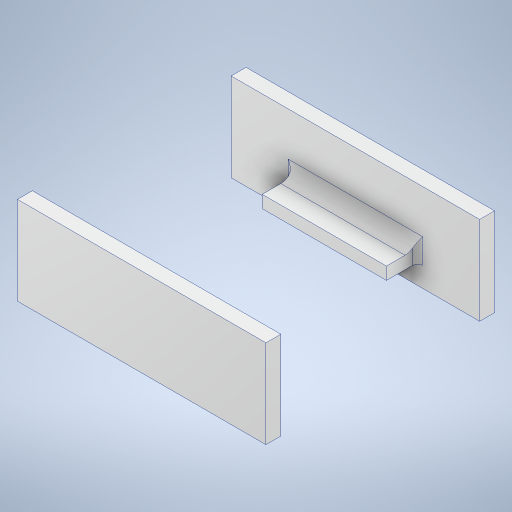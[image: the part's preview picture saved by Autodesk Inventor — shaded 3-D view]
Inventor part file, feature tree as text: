
AUTODESK INVENTOR PART (.ipt)
format: ipt  version: 2024 (Build 280153000, 153)  size: 330,240 bytes
history: native  units: mm
features: extrude x6, sketch x6, projected_geometry x3, fillet x2
ambient origin geometry x8: Origin, YZ Plane, XZ Plane, XY Plane, X Axis, Y Axis, Z Axis, Center Point
bodies: Solid1 (feature_tree)
feature tree (17):
  extrude  "Extrusion1"  Depth=200.0mm
  extrude  "Extrusion2"  Depth=60.0mm
  extrude  "Extrusion3"  Depth=12.0mm
  extrude  "Extrusion6"  Depth=25.0mm TaperAngle=0.0deg
  fillet  "Fillet1"  Radius=12.0mm
  fillet  "Fillet2"  Radius=25.0mm
  extrude  "Extrusion7"  Depth=50.0mm
  extrude  "Extrusion8"  Depth=50.0mm
  sketch  "Sketch1"  dims[d0=160.0mm d1=200.0mm]
  sketch  "Sketch2"  dims[d2=11.0mm d3=0.0mm d4=60.0mm]
  sketch  "Sketch3"  dims[d5=60.0mm d6=12.0mm]
  projected_geometry  "Projected Loop1"
  sketch  "Sketch7"  dims[d7=10.0mm d8=0.0mm d9=5.0mm d10=0.0mm d17=12.0mm d18=25.0mm]
  sketch  "Sketch8"  dims[d19=25.0mm d20=50.0mm]
  sketch  "Sketch10"  dims[d21=50.0mm d22=50.0mm d23=50.0mm d24=10.0mm d25=0.0mm d26=4.0mm d27=10.0mm d28=1000.0mm d29=0.0mm d31=6.0mm d32=0.0mm]
  projected_geometry  "Projected Loop3"
  projected_geometry  "Projected Loop4"
